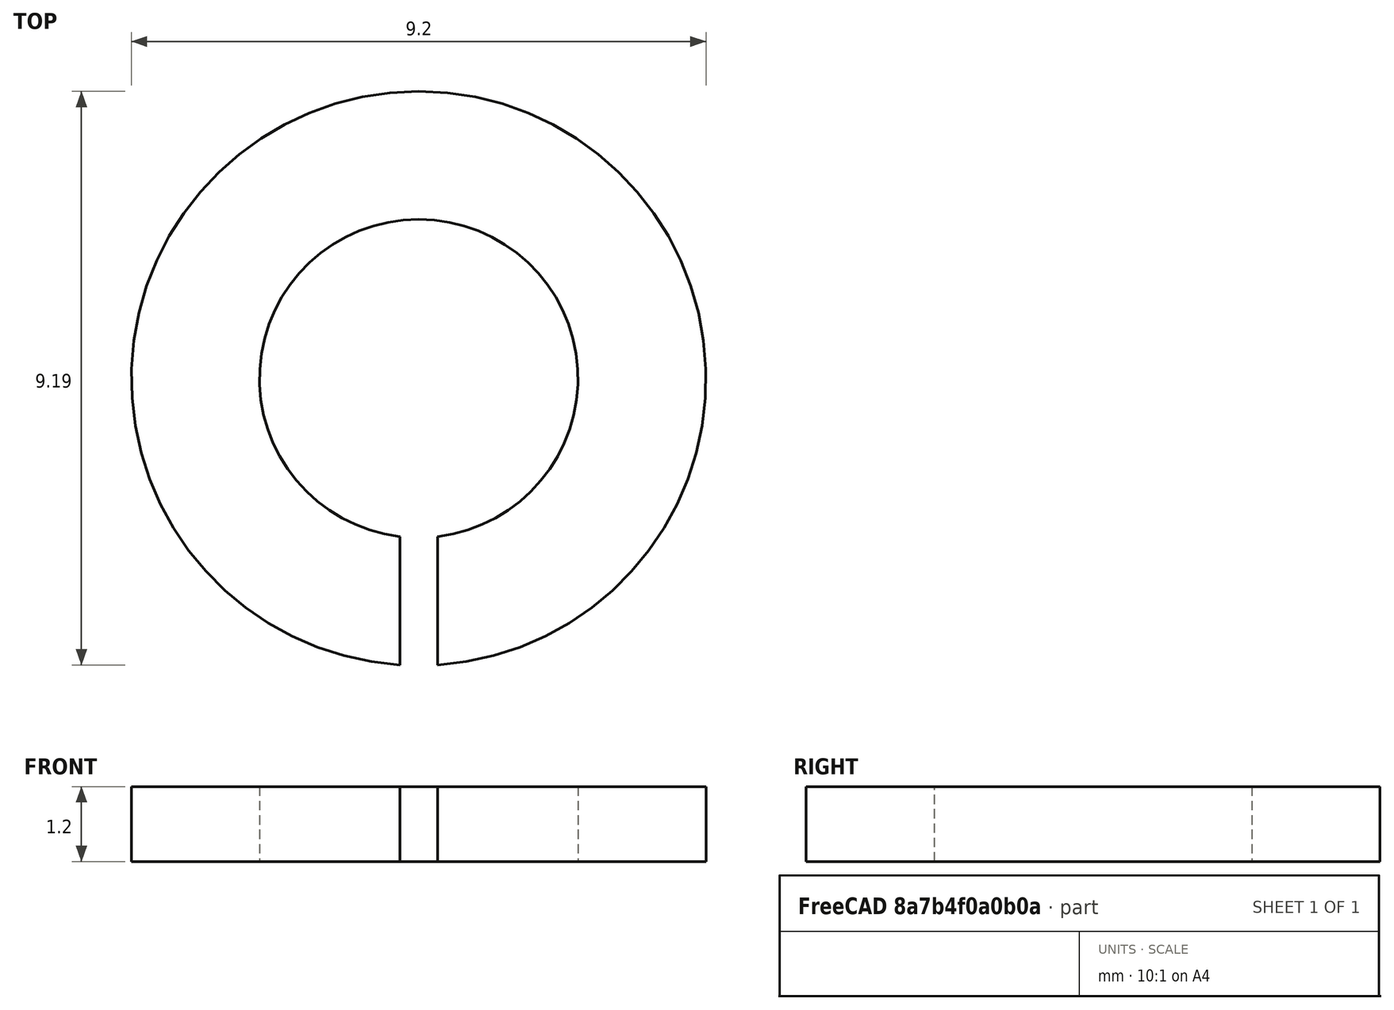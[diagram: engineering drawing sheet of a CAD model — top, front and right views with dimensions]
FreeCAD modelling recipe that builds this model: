
FCSTD DOCUMENT  (FreeCAD 0.15R4651 (Git))
Label: Federring_DIN127-A5
License: All rights reserved
LicenseURL: http://de.wikipedia.org/wiki/Alle_Rechte_vorbehalten
objects: Sketcher::SketchObject×1, PartDesign::Pad×1
note: 3 computed .brp shape members not serialized (recipe doc carries the construction recipe); baked Part::Feature solids carry a one-line shape summary decoded from their .brp

FEATURE [Sketcher::SketchObject] Sketch
  sketch-geometry (4):
    g0: ArcOfCircle CenterX=0 CenterY=0 CenterZ=0 NormalX=0 NormalY=0 NormalZ=1 Radius=2.55 StartAngle=4.83031 EndAngle=10.8777
    g1: ArcOfCircle CenterX=0 CenterY=0 CenterZ=0 NormalX=0 NormalY=0 NormalZ=1 Radius=4.6 StartAngle=4.77765 EndAngle=10.9303
    g2: LineSegment StartX=0.3 StartY=-2.53229 StartZ=0 EndX=0.3 EndY=-4.59021 EndZ=0
    g3: LineSegment StartX=-0.3 StartY=-4.59021 StartZ=0 EndX=-0.3 EndY=-2.53229 EndZ=0
  constraints (12):
    c: Coincident(g0,g-1)
    c: Coincident(g1,g-1)
    c: Vertical(g2)
    c: Vertical(g3)
    c: Coincident(g0,g2)
    c: Coincident(g0,g3)
    c: Coincident(g1,g2)
    c: Coincident(g1,g3)
    c: Symmetric(g1,g1,g-2)
    c: Radius(g0) = 2.55
    c: Radius(g1) = 4.6
    c: DistanceX(g1,g1) = -0.6
FEATURE [PartDesign::Pad] Pad  label="Federring DIN 127-A 5 #"
  Length = 1.2
  Length2 = 100
  Midplane = true
  Sketch = -> Sketch
  Type = 0
